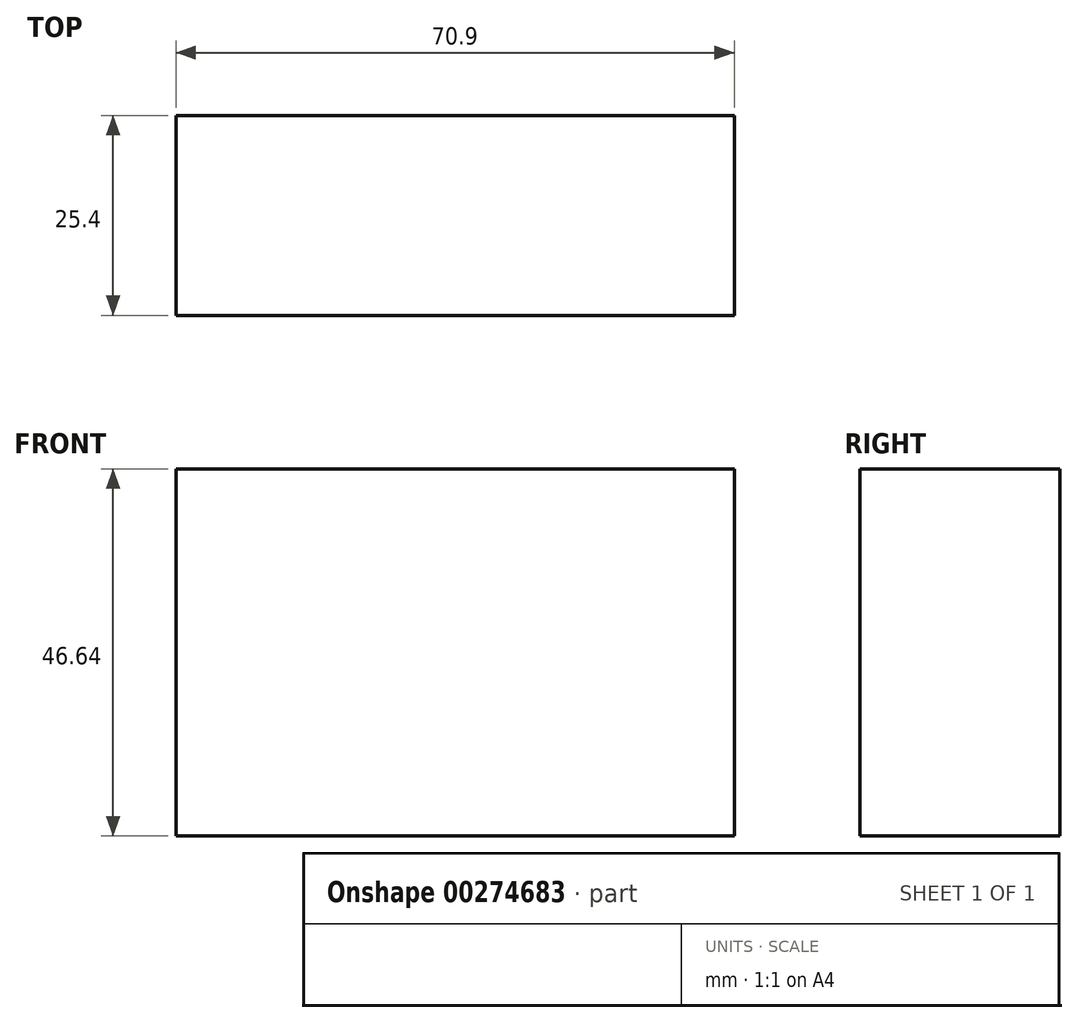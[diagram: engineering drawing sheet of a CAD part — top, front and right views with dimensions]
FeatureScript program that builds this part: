
annotation { "Feature Type Name" : "Feature", "Feature Type Description" : "" }
export const myFeature = defineFeature(function(context is Context, id is Id, definition is map)
    precondition{}
    {
        {
            var Q0;
            Q0=qCreatedBy(makeId("Front.planeOp"),FACE);
            var sketch = newSketch(context, id + "F0", { "sketchPlane" : qUnion([Q0])});
            skLineSegment(sketch, "E0.bottom", {"start": v(35.45, 23.32) * mm, "end": v(-35.45, 23.32) * mm});
            skLineSegment(sketch, "E0.top", {"start": v(35.45, -23.32) * mm, "end": v(-35.45, -23.32) * mm});
            skLineSegment(sketch, "E0.left", {"start": v(35.45, 23.32) * mm, "end": v(35.45, -23.32) * mm});
            skLineSegment(sketch, "E0.right", {"start": v(-35.45, 23.32) * mm, "end": v(-35.45, -23.32) * mm});
            skPoint(sketch, "E0.middle", {"position": v(0, 0) * mm});
            skSolve(sketch);
        }
        {
            var Q0;
            Q0 = qSketchRegion(id + "F0", true);
            extrude(context, id + "F1", {"entities" : qUnion([Q0]), "depth" : 25.4 * mm});
        }
    });
